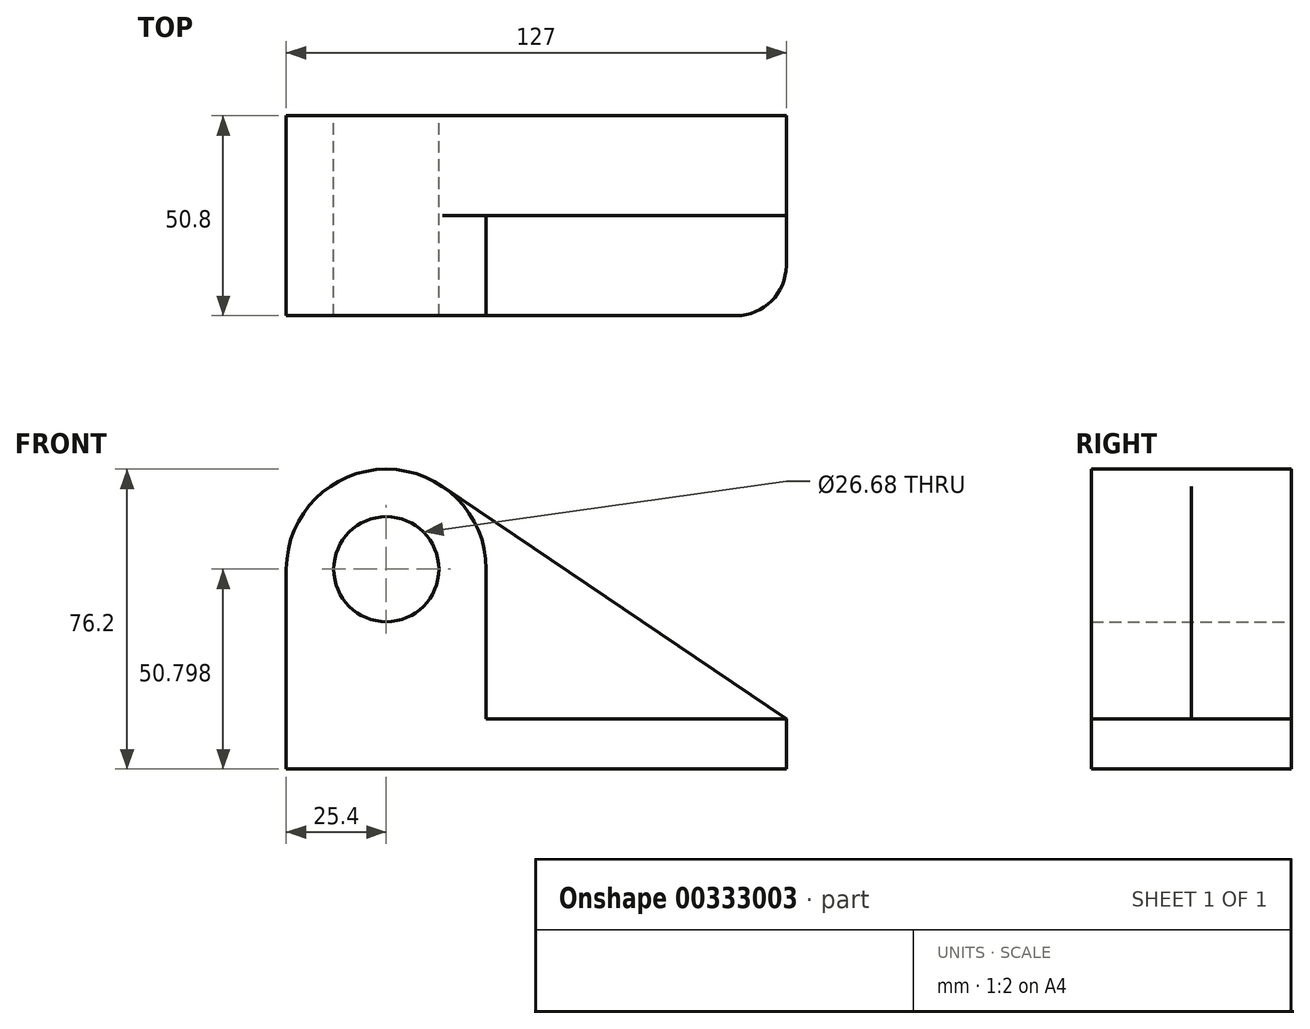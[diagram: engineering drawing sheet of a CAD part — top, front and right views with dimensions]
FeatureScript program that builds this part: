
annotation { "Feature Type Name" : "Feature", "Feature Type Description" : "" }
export const myFeature = defineFeature(function(context is Context, id is Id, definition is map)
    precondition{}
    {
        {
            var Q0;
            Q0=qCreatedBy(makeId("Front.planeOp"),FACE);
            var sketch = newSketch(context, id + "F0", { "sketchPlane" : qUnion([Q0])});
            skArc(sketch, "E0", {"start": v(-38.2, 27.56) * mm, "mid": v(-64.35, 28.96) * mm, "end": v(-77.84, 6.53) * mm});
            skCircle(sketch, "E1", {"center": v(-52.44, 6.53) * mm, "radius": 13.34 * mm});
            skLineSegment(sketch, "E2", {"start": v(-77.84, -44.27) * mm, "end": v(49.16, -44.27) * mm});
            skLineSegment(sketch, "E3", {"start": v(49.16, -44.27) * mm, "end": v(49.16, -31.57) * mm});
            skLineSegment(sketch, "E4", {"start": v(49.16, -31.57) * mm, "end": v(-38.2, 27.56) * mm});
            skLineSegment(sketch, "E5", {"start": v(-77.84, 6.53) * mm, "end": v(-77.84, -44.27) * mm});
            skSolve(sketch);
        }
        {
            var Q0;
            Q0 = qSketchRegion(id + "F0", true);
            extrude(context, id + "F1", {"entities" : qUnion([Q0]), "depth" : 25.4 * mm});
        }
        {
            var Q0;
            Q0=makeQuery(id+"F1.opExtrude","CAP_FACE",FACE,{"disambiguationData":[OSD([sQuery(id+"F0.wireOp",EDGE,"E0"),sQuery(id+"F0.wireOp",EDGE,"E1"),sQuery(id+"F0.wireOp",EDGE,"E2"),sQuery(id+"F0.wireOp",EDGE,"E3"),sQuery(id+"F0.wireOp",EDGE,"E4"),sQuery(id+"F0.wireOp",EDGE,"E5")])],"isStart":false});
            var sketch = newSketch(context, id + "F2", { "sketchPlane" : qUnion([Q0])});
            skCircle(sketch, "E6", {"center": v(-52.44, 6.53) * mm, "radius": 12.7 * mm});
            skArc(sketch, "E7", {"start": v(-27.04, 6.53) * mm, "mid": v(-52.44, 31.93) * mm, "end": v(-77.84, 6.53) * mm});
            skLineSegment(sketch, "E8.bottom", {"start": v(49.16, -31.57) * mm, "end": v(-27.04, -31.57) * mm});
            skLineSegment(sketch, "E8.top", {"start": v(49.16, -44.27) * mm, "end": v(-77.84, -44.27) * mm});
            skLineSegment(sketch, "E8.left", {"start": v(49.16, -31.57) * mm, "end": v(49.16, -44.27) * mm});
            skLineSegment(sketch, "E8.right", {"start": v(-77.84, -31.57) * mm, "end": v(-77.84, -44.27) * mm});
            skLineSegment(sketch, "E9", {"start": v(-77.84, 6.53) * mm, "end": v(-77.84, -31.57) * mm});
            skLineSegment(sketch, "E10", {"start": v(-27.04, 6.53) * mm, "end": v(-27.04, -31.57) * mm});
            skSolve(sketch);
        }
        {
            var Q0;
            Q0=makeQuery(id+"F2.imprint","IMPRINT",FACE,{"disambiguationData":[TD([[makeQuery(id+"F2.imprint","IMPRINT",EDGE,{"derivedFrom":sQuery(id+"F2.wireOp",EDGE,"E8.bottom")}),1.0]])]});
            extrude(context, id + "F3", {"entities" : qUnion([Q0]), "operationType" : NewBodyOperationType.ADD, "depth" : 25.4 * mm});
        }
        {
            var Q0;
            Q0=makeQuery(id+"F3.opExtrude","CAP_EDGE",EDGE,{"disambiguationData":[OSD([sQuery(id+"F2.wireOp",EDGE,"E8.left")])],"isStart":false});
            fillet(context, id + "F4", {"entities" : qUnion([Q0]), "radius" : 12.7 * mm, "tangentPropagation" : true, "allowEdgeOverflow" : false});
        }
    });
